# Revit family: BC_Hitachi_RPK-2-4FSRM_LOD400
name_source: partatom
category: Mechanical Equipment
revit_build: Autodesk Revit 2018 (Build: 20170223_1515(x64)
units: mm (PartAtom-declared; Revit-internal decimal feet)

## family parameters
Cut with Voids When Loaded = No
Host = Face
OmniClass Number = 23.75.00.00
OmniClass Title = Climate Control (HVAC)
Part Type = Normal
Room Calculation Point = No
Round Connector Dimension = Use Diameter
Shared = No

## types (4) — shared parameters
BC_OBJECT_ID = 209118
BC_OBJECT_VERSION = #9
Default Elevation = 1219.20 mm
Description = Wall Hung without electronic expansion valve inside
Diameter left side pipe wire hole = 65.00 mm
Diameter right side pipe wire hole = 65.00 mm
Distance Gas pipe = 107.00 mm
Distance rear left side pipe wire hole = 136.00 mm
Distance rear right side pipe wire hole = 107.00 mm
Engine Power = 40 W
Frequency = 50 Hz
Manufacturer = Hitachi Air Conditioning Europe SAS
MasterFormat = Indoor Central-Station Air-Handling Units
Masterformat Code = 23 73 00
Maximum Current = 5 A
Model = Indoor unit - Wall hung RPK- 2-4 FSRM
Name BIM&CO = Indoor Unit
Nominal Voltage = 230 V
Number of Poles = 1
OmniClass code = 23-33 25 00
OmniClass description = Air Handling Units
Operation and service space = Yes
Operation and service space - Material = Operation and service space
Operation and service space - a = 100.00 mm
Operation and service space - b = 200.00 mm
Operation and service space - c = 100.00 mm
Operation and service space - d = 1000.00 mm
Outlet Diameter = 20.00 mm
Overall depth = 260.00 mm
Overall height = 300.00 mm
Overall width = 1100.00 mm
Packaging volume = 0.14 m³
Refrigerant Type = R410A / R32
Refrigerant pipe connection = Flare nuts
Remote control = PC-ARFP1E / PC-AWR (*)
Uniformat = Distribution Systems
Uniformat code = D3040

## per-type parameters (varying)
| type | Air Flow - Speed Hi | Air Flow - Speed Medium | BC_VARIANT_ID | Cooling Capacity | Gas Diameter | Heating Capacity | Liquid Diameter | Maximum Air Flow | Minimum Air Flow | Net Weight | Nominal cooling capacity (UTOPIA) | Nominal heating capacity (UTOPIA) | Product Code | Reference | Sound Power Min | Sound power level - Speed Hi2 (dB(A)) | Sound power level - Speed Medium (dB(A)) | Sound pressure level - Speed Hi (dB(A)) | Sound pressure level - Speed Hi2 (dB(A)) | Sound pressure level - Speed Low (dB(A)) | Sound pressure level - Speed Medium (dB(A)) |
| RPK-2.0FSRM | 780.0 m³/h | 660.0 m³/h | 508766 | 6 kW | 12.70 mm | 6 kW | 6.35 mm | 1380.0 m³/h | 870.0 m³/h | 14.50 kg | 5 kW | 6 kW | 60279209 | RPK-2.0FSRM | 47 | 55 | 50 | 37 | 40 | 34 | 31 |
| RPK-2.5FSRM | 990.0 m³/h | 840.0 m³/h | 508763 | 6 kW | 15.88 mm | 6 kW | 9.52 mm | 870.0 m³/h | 570.0 m³/h | 15.00 kg | 6 kW | 6 kW | 60279212 | RPK-2.0FSRM | 54 | 60 | 54 | 42 | 45 | 38 | 35 |
| RPK-3.0FSRM | 1050.0 m³/h | 930.0 m³/h | 508764 | 8 kW | 15.88 mm | 9 kW | 9.52 mm | 1100.0 m³/h | 720.0 m³/h | 15.00 kg | 7 kW | 8 kW | 60279211 | RPK-3.0FSRM | 51 | 63 | 56 | 44 | 47 | 40 | 35 |
| RPK-4.0FSRM | 1200.0 m³/h | 1050.0 m³/h | 508765 | 8 kW | 15.88 mm | 9 kW | 9.52 mm | 1200.0 m³/h | 750.0 m³/h | 15.00 kg | 7 kW | 8 kW | 60279212 | RPK-4.0FSRM | 54 | 65 | 60 | 48 | 51 | 44 | 39 |

note: column(s) folded — value = type name in every type: Type Comments
